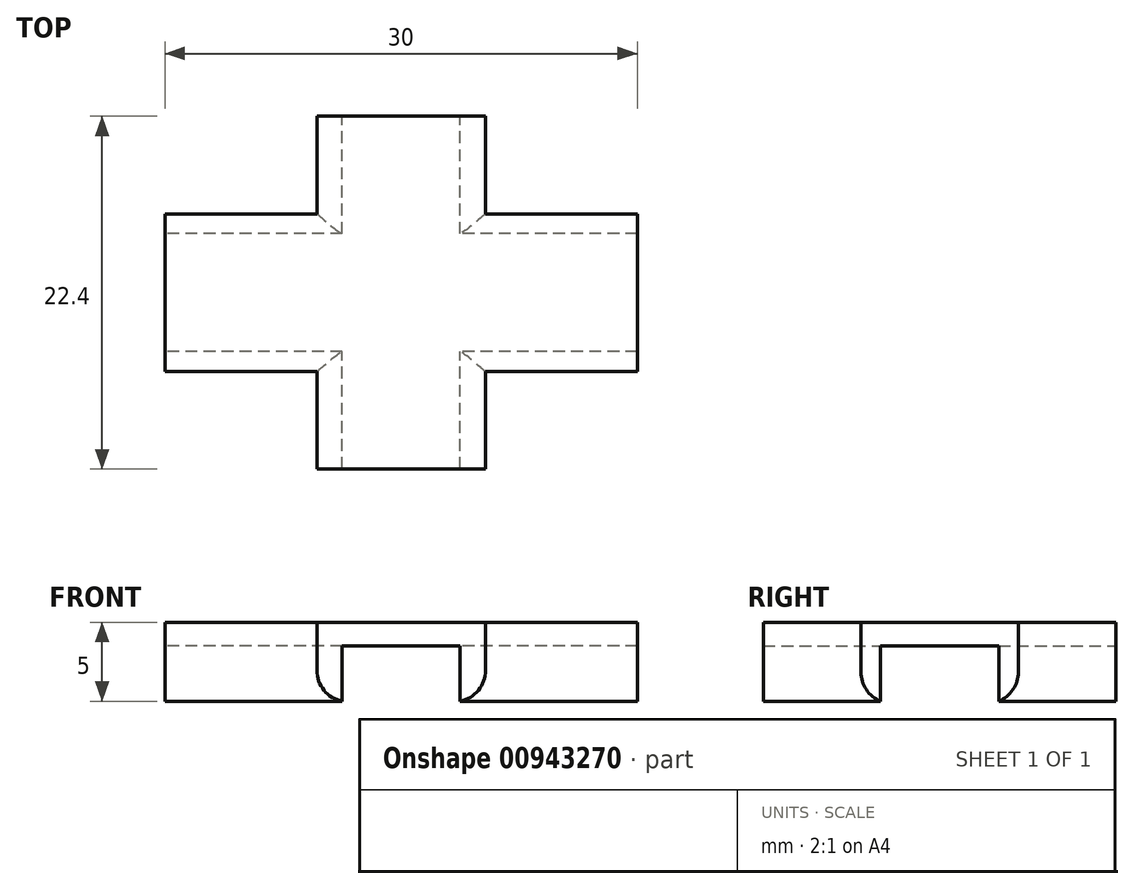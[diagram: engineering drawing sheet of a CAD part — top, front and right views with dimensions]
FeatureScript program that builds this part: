
annotation { "Feature Type Name" : "Feature", "Feature Type Description" : "" }
export const myFeature = defineFeature(function(context is Context, id is Id, definition is map)
    precondition{}
    {
        {
            var Q0;
            Q0=qCreatedBy(makeId("Top.planeOp"),FACE);
            var sketch = newSketch(context, id + "F0", { "sketchPlane" : qUnion([Q0])});
            skLineSegment(sketch, "E0.bottom", {"start": v(3.75, -11.2) * mm, "end": v(-3.75, -11.2) * mm});
            skLineSegment(sketch, "E0.top", {"start": v(3.75, 11.2) * mm, "end": v(-3.75, 11.2) * mm});
            skLineSegment(sketch, "E0.left", {"start": v(3.75, -11.2) * mm, "end": v(3.75, -3.75) * mm});
            skLineSegment(sketch, "E0.right", {"start": v(-3.75, -11.2) * mm, "end": v(-3.75, -3.75) * mm});
            skPoint(sketch, "E0.middle", {"position": v(0, 0) * mm});
            skLineSegment(sketch, "E1.bottom", {"start": v(15, -3.75) * mm, "end": v(3.75, -3.75) * mm});
            skLineSegment(sketch, "E1.top", {"start": v(15, 3.75) * mm, "end": v(3.75, 3.75) * mm});
            skLineSegment(sketch, "E1.left", {"start": v(15, -3.75) * mm, "end": v(15, 3.75) * mm});
            skLineSegment(sketch, "E1.right", {"start": v(-15, -3.75) * mm, "end": v(-15, 3.75) * mm});
            skLineSegment(sketch, "E2.trimOffspring", {"start": v(-3.75, 3.75) * mm, "end": v(-3.75, 11.2) * mm});
            skLineSegment(sketch, "E3.trimOffspring", {"start": v(3.75, 3.75) * mm, "end": v(3.75, 11.2) * mm});
            skLineSegment(sketch, "E4.trimOffspring", {"start": v(-3.75, 3.75) * mm, "end": v(-15, 3.75) * mm});
            skLineSegment(sketch, "E5.trimOffspring", {"start": v(-3.75, -3.75) * mm, "end": v(-15, -3.75) * mm});
            skSolve(sketch);
        }
        {
            var Q0;
            Q0=qCreatedBy(makeId("Top.planeOp"),FACE);
            var sketch = newSketch(context, id + "F1", { "sketchPlane" : qUnion([Q0])});
            skLineSegment(sketch, "E6.bottom", {"start": v(5.35, -11.2) * mm, "end": v(-5.35, -11.2) * mm});
            skLineSegment(sketch, "E6.top", {"start": v(5.35, 11.2) * mm, "end": v(-5.35, 11.2) * mm});
            skLineSegment(sketch, "E6.left", {"start": v(5.35, -11.2) * mm, "end": v(5.35, -5) * mm});
            skLineSegment(sketch, "E6.right", {"start": v(-5.35, -11.2) * mm, "end": v(-5.35, -5) * mm});
            skPoint(sketch, "E6.middle", {"position": v(0, 0) * mm});
            skLineSegment(sketch, "E7.bottom", {"start": v(15, -5) * mm, "end": v(5.35, -5) * mm});
            skLineSegment(sketch, "E7.top", {"start": v(15, 5) * mm, "end": v(5.35, 5) * mm});
            skLineSegment(sketch, "E7.left", {"start": v(15, -5) * mm, "end": v(15, 5) * mm});
            skLineSegment(sketch, "E7.right", {"start": v(-15, -5) * mm, "end": v(-15, 5) * mm});
            skLineSegment(sketch, "E8.trimOffspring", {"start": v(-5.35, 5) * mm, "end": v(-15, 5) * mm});
            skLineSegment(sketch, "E9.trimOffspring", {"start": v(-5.35, -5) * mm, "end": v(-15, -5) * mm});
            skLineSegment(sketch, "E10.trimOffspring", {"start": v(-5.35, 5) * mm, "end": v(-5.35, 11.2) * mm});
            skLineSegment(sketch, "E11.trimOffspring", {"start": v(5.35, 5) * mm, "end": v(5.35, 11.2) * mm});
            skSolve(sketch);
        }
        {
            var Q0;
            Q0 = qSketchRegion(id + "F1", true);
            extrude(context, id + "F2", {"entities" : qUnion([Q0]), "depth" : 5 * mm, "offsetDistance" : 25 * mm});
        }
        {
            var Q0;
            Q0 = qSketchRegion(id + "F0", true);
            extrude(context, id + "F3", {"entities" : qUnion([Q0]), "operationType" : NewBodyOperationType.REMOVE, "depth" : 3.5 * mm, "offsetDistance" : 25 * mm});
        }
        {
            var Q0;
            Q0=makeQuery(id+"F2.opExtrude","CAP_EDGE",EDGE,{"disambiguationData":[OSD([sQuery(id+"F1.wireOp",EDGE,"E7.top")])],"isStart":true});
            var Q1;
            Q1=makeQuery(id+"F2.opExtrude","CAP_EDGE",EDGE,{"disambiguationData":[OSD([sQuery(id+"F1.wireOp",EDGE,"E10.trimOffspring")])],"isStart":true});
            var Q2;
            Q2=makeQuery(id+"F2.opExtrude","CAP_EDGE",EDGE,{"disambiguationData":[OSD([sQuery(id+"F1.wireOp",EDGE,"E11.trimOffspring")])],"isStart":true});
            var Q3;
            Q3=makeQuery(id+"F2.opExtrude","CAP_EDGE",EDGE,{"disambiguationData":[OSD([sQuery(id+"F1.wireOp",EDGE,"E8.trimOffspring")])],"isStart":true});
            var Q4;
            Q4=makeQuery(id+"F2.opExtrude","CAP_EDGE",EDGE,{"disambiguationData":[OSD([sQuery(id+"F1.wireOp",EDGE,"E9.trimOffspring")])],"isStart":true});
            var Q5;
            Q5=makeQuery(id+"F2.opExtrude","CAP_EDGE",EDGE,{"disambiguationData":[OSD([sQuery(id+"F1.wireOp",EDGE,"E6.right")])],"isStart":true});
            var Q6;
            Q6=makeQuery(id+"F2.opExtrude","CAP_EDGE",EDGE,{"disambiguationData":[OSD([sQuery(id+"F1.wireOp",EDGE,"E6.left")])],"isStart":true});
            var Q7;
            Q7=makeQuery(id+"F2.opExtrude","CAP_EDGE",EDGE,{"disambiguationData":[OSD([sQuery(id+"F1.wireOp",EDGE,"E7.bottom")])],"isStart":true});
            fillet(context, id + "F4", {"entities" : qUnion([Q0, Q1, Q2, Q3, Q4, Q5, Q6, Q7]), "radius" : 2 * mm, "tangentPropagation" : true, "allowEdgeOverflow" : false});
        }
    });
